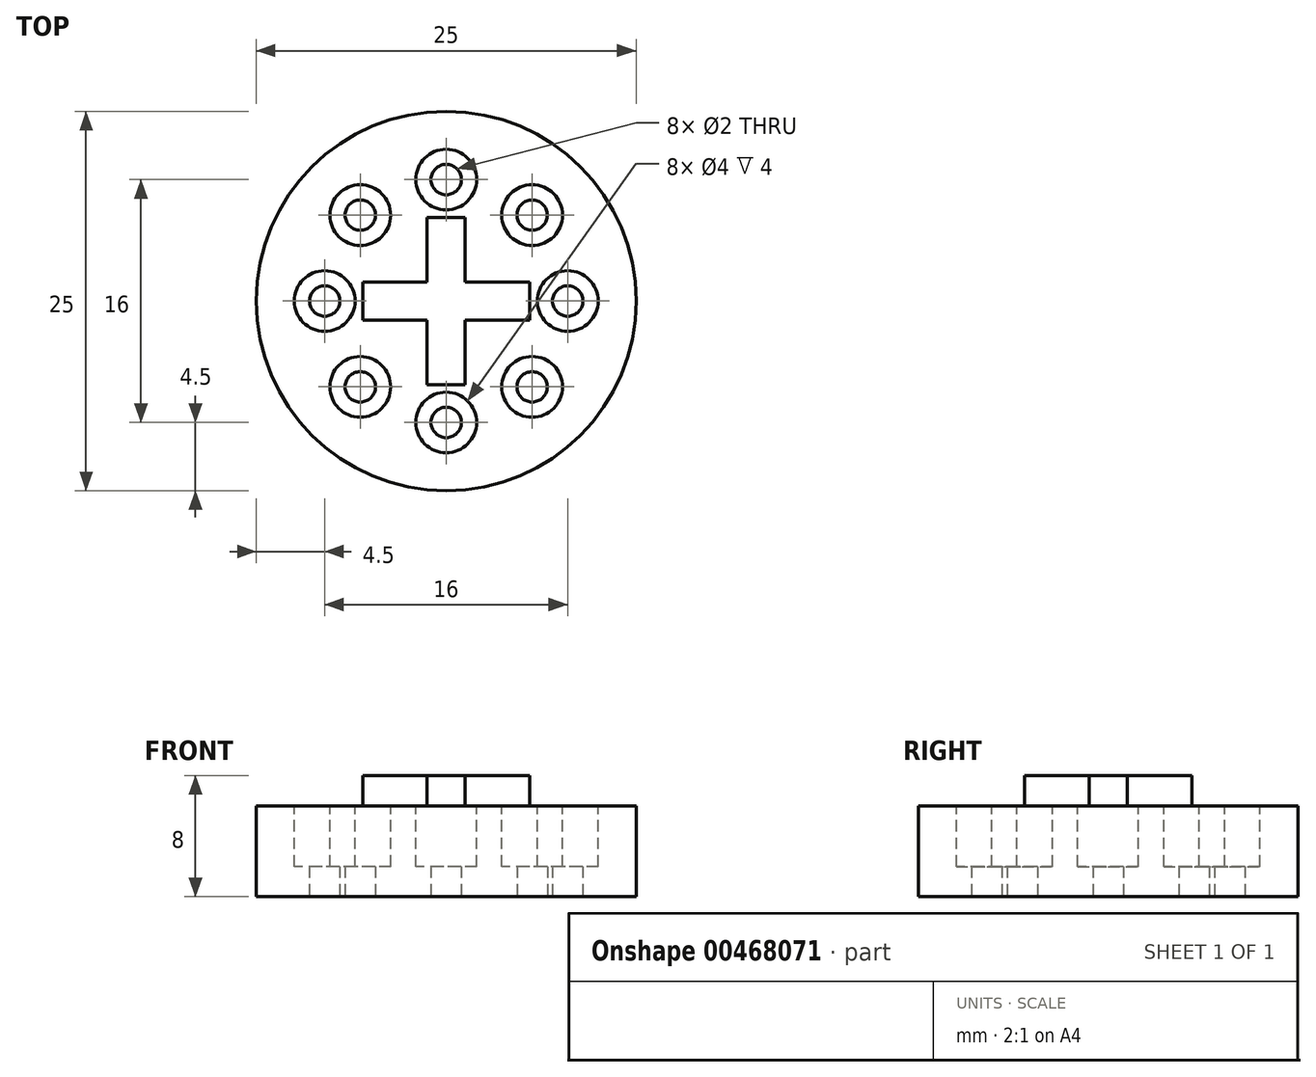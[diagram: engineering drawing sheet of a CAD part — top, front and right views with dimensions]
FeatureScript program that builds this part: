
annotation { "Feature Type Name" : "Feature", "Feature Type Description" : "" }
export const myFeature = defineFeature(function(context is Context, id is Id, definition is map)
    precondition{}
    {
        {
            var Q0;
            Q0=qCreatedBy(makeId("Top.planeOp"),FACE);
            var sketch = newSketch(context, id + "F0", { "sketchPlane" : qUnion([Q0])});
            skCircle(sketch, "E0", {"center": v(0, 0) * mm, "radius": 12.5 * mm});
            skSolve(sketch);
        }
        {
            var Q0;
            Q0 = qSketchRegion(id + "F0", true);
            extrude(context, id + "F1", {"entities" : qUnion([Q0]), "endBound" : BoundingType.SYMMETRIC, "depth" : 6 * mm});
        }
        {
            var Q0;
            Q0=qCreatedBy(makeId("Top.planeOp"),FACE);
            var sketch = newSketch(context, id + "F2", { "sketchPlane" : qUnion([Q0])});
            skCircle(sketch, "E1", {"center": v(0, 0) * mm, "radius": 12.5 * mm});
            skCircle(sketch, "E2", {"center": v(-8, 0) * mm, "radius": 1 * mm});
            skCircle(sketch, "E3.1.0", {"center": v(-5.66, -5.66) * mm, "radius": 1 * mm});
            skCircle(sketch, "E3.2.0", {"center": v(0, -8) * mm, "radius": 1 * mm});
            skCircle(sketch, "E3.3.0", {"center": v(5.66, -5.66) * mm, "radius": 1 * mm});
            skCircle(sketch, "E3.4.0", {"center": v(8, 0) * mm, "radius": 1 * mm});
            skCircle(sketch, "E3.5.0", {"center": v(5.66, 5.66) * mm, "radius": 1 * mm});
            skCircle(sketch, "E3.6.0", {"center": v(0, 8) * mm, "radius": 1 * mm});
            skCircle(sketch, "E3.7.0", {"center": v(-5.66, 5.66) * mm, "radius": 1 * mm});
            skSolve(sketch);
        }
        {
            var Q0;
            Q0=makeQuery(id+"F2.imprint","IMPRINT",FACE,{"disambiguationData":[TD([[makeQuery(id+"F2.imprint","IMPRINT",EDGE,{"derivedFrom":sQuery(id+"F2.wireOp",EDGE,"E3.2.0")}),1.0]])]});
            var Q1;
            Q1=makeQuery(id+"F2.imprint","IMPRINT",FACE,{"disambiguationData":[TD([[makeQuery(id+"F2.imprint","IMPRINT",EDGE,{"derivedFrom":sQuery(id+"F2.wireOp",EDGE,"E3.1.0")}),1.0]])]});
            var Q2;
            Q2=makeQuery(id+"F2.imprint","IMPRINT",FACE,{"disambiguationData":[TD([[makeQuery(id+"F2.imprint","IMPRINT",EDGE,{"derivedFrom":sQuery(id+"F2.wireOp",EDGE,"E2")}),1.0]])]});
            var Q3;
            Q3=makeQuery(id+"F2.imprint","IMPRINT",FACE,{"disambiguationData":[TD([[makeQuery(id+"F2.imprint","IMPRINT",EDGE,{"derivedFrom":sQuery(id+"F2.wireOp",EDGE,"E3.7.0")}),1.0]])]});
            var Q4;
            Q4=makeQuery(id+"F2.imprint","IMPRINT",FACE,{"disambiguationData":[TD([[makeQuery(id+"F2.imprint","IMPRINT",EDGE,{"derivedFrom":sQuery(id+"F2.wireOp",EDGE,"E3.6.0")}),1.0]])]});
            var Q5;
            Q5=makeQuery(id+"F2.imprint","IMPRINT",FACE,{"disambiguationData":[TD([[makeQuery(id+"F2.imprint","IMPRINT",EDGE,{"derivedFrom":sQuery(id+"F2.wireOp",EDGE,"E3.5.0")}),1.0]])]});
            var Q6;
            Q6=makeQuery(id+"F2.imprint","IMPRINT",FACE,{"disambiguationData":[TD([[makeQuery(id+"F2.imprint","IMPRINT",EDGE,{"derivedFrom":sQuery(id+"F2.wireOp",EDGE,"E3.4.0")}),1.0]])]});
            var Q7;
            Q7=makeQuery(id+"F2.imprint","IMPRINT",FACE,{"disambiguationData":[TD([[makeQuery(id+"F2.imprint","IMPRINT",EDGE,{"derivedFrom":sQuery(id+"F2.wireOp",EDGE,"E3.3.0")}),1.0]])]});
            var Q8;
            Q8=sQuery(id+"F2.wireOp",EDGE,"E3.7.0");
            var Q9;
            Q9=sQuery(id+"F2.wireOp",EDGE,"E2");
            var Q10;
            Q10=sQuery(id+"F2.wireOp",EDGE,"E3.6.0");
            var Q11;
            Q11=sQuery(id+"F2.wireOp",EDGE,"E3.5.0");
            var Q12;
            Q12=sQuery(id+"F2.wireOp",EDGE,"E3.4.0");
            var Q13;
            Q13=sQuery(id+"F2.wireOp",EDGE,"E3.2.0");
            var Q14;
            Q14=sQuery(id+"F2.wireOp",EDGE,"E3.3.0");
            var Q15;
            Q15=sQuery(id+"F2.wireOp",EDGE,"E3.1.0");
            extrude(context, id + "F3", {"entities" : qUnion([Q0, Q1, Q2, Q3, Q4, Q5, Q6, Q7]), "operationType" : NewBodyOperationType.REMOVE, "surfaceEntities" : qUnion([Q8, Q9, Q10, Q11, Q12, Q13, Q14, Q15]), "endBound" : BoundingType.SYMMETRIC, "depth" : 25 * mm});
        }
        {
            var Q0;
            Q0=makeQuery(id+"F1.opExtrude","CAP_FACE",FACE,{"disambiguationData":[OSD([sQuery(id+"F0.wireOp",EDGE,"E0")])],"isStart":false});
            var sketch = newSketch(context, id + "F4", { "sketchPlane" : qUnion([Q0])});
            skCircle(sketch, "E4", {"center": v(-5.66, 5.66) * mm, "radius": 2 * mm});
            skCircle(sketch, "E5.1.0", {"center": v(-8, 0) * mm, "radius": 2 * mm});
            skCircle(sketch, "E5.2.0", {"center": v(-5.66, -5.66) * mm, "radius": 2 * mm});
            skCircle(sketch, "E5.3.0", {"center": v(0, -8) * mm, "radius": 2 * mm});
            skCircle(sketch, "E5.4.0", {"center": v(5.66, -5.66) * mm, "radius": 2 * mm});
            skCircle(sketch, "E5.5.0", {"center": v(8, 0) * mm, "radius": 2 * mm});
            skCircle(sketch, "E5.6.0", {"center": v(5.66, 5.66) * mm, "radius": 2 * mm});
            skCircle(sketch, "E5.7.0", {"center": v(0, 8) * mm, "radius": 2 * mm});
            skPoint(sketch, "E5.center", {"position": v(0, 0) * mm});
            skSolve(sketch);
        }
        {
            var Q0;
            Q0=makeQuery(id+"F4.imprint","IMPRINT",FACE,{"disambiguationData":[TD([[makeQuery(id+"F4.imprint","IMPRINT",EDGE,{"derivedFrom":sQuery(id+"F4.wireOp",EDGE,"E4")}),1.0]])]});
            var Q1;
            Q1=makeQuery(id+"F4.imprint","IMPRINT",FACE,{"disambiguationData":[TD([[makeQuery(id+"F4.imprint","IMPRINT",EDGE,{"derivedFrom":sQuery(id+"F4.wireOp",EDGE,"E5.1.0")}),1.0]])]});
            var Q2;
            Q2=makeQuery(id+"F4.imprint","IMPRINT",FACE,{"disambiguationData":[TD([[makeQuery(id+"F4.imprint","IMPRINT",EDGE,{"derivedFrom":sQuery(id+"F4.wireOp",EDGE,"E5.7.0")}),1.0]])]});
            var Q3;
            Q3=makeQuery(id+"F4.imprint","IMPRINT",FACE,{"disambiguationData":[TD([[makeQuery(id+"F4.imprint","IMPRINT",EDGE,{"derivedFrom":sQuery(id+"F4.wireOp",EDGE,"E5.5.0")}),1.0]])]});
            var Q4;
            Q4=makeQuery(id+"F4.imprint","IMPRINT",FACE,{"disambiguationData":[TD([[makeQuery(id+"F4.imprint","IMPRINT",EDGE,{"derivedFrom":sQuery(id+"F4.wireOp",EDGE,"E5.6.0")}),1.0]])]});
            var Q5;
            Q5=makeQuery(id+"F4.imprint","IMPRINT",FACE,{"disambiguationData":[TD([[makeQuery(id+"F4.imprint","IMPRINT",EDGE,{"derivedFrom":sQuery(id+"F4.wireOp",EDGE,"E5.4.0")}),1.0]])]});
            var Q6;
            Q6=makeQuery(id+"F4.imprint","IMPRINT",FACE,{"disambiguationData":[TD([[makeQuery(id+"F4.imprint","IMPRINT",EDGE,{"derivedFrom":sQuery(id+"F4.wireOp",EDGE,"E5.3.0")}),1.0]])]});
            var Q7;
            Q7=makeQuery(id+"F4.imprint","IMPRINT",FACE,{"disambiguationData":[TD([[makeQuery(id+"F4.imprint","IMPRINT",EDGE,{"derivedFrom":sQuery(id+"F4.wireOp",EDGE,"E5.2.0")}),1.0]])]});
            extrude(context, id + "F5", {"entities" : qUnion([Q0, Q1, Q2, Q3, Q4, Q5, Q6, Q7]), "operationType" : NewBodyOperationType.REMOVE, "oppositeDirection" : true, "depth" : 4 * mm});
        }
        {
            var Q0;
            Q0=makeQuery(id+"F1.opExtrude","CAP_FACE",FACE,{"disambiguationData":[OSD([sQuery(id+"F0.wireOp",EDGE,"E0")])],"isStart":false});
            var sketch = newSketch(context, id + "F6", { "sketchPlane" : qUnion([Q0])});
            skLineSegment(sketch, "E6.bottom", {"start": v(-1.25, 5.5) * mm, "end": v(1.25, 5.5) * mm});
            skLineSegment(sketch, "E6.top", {"start": v(-1.25, -5.5) * mm, "end": v(1.25, -5.5) * mm});
            skLineSegment(sketch, "E6.left", {"start": v(-1.25, 5.5) * mm, "end": v(-1.25, -5.5) * mm});
            skLineSegment(sketch, "E6.right", {"start": v(1.25, 5.5) * mm, "end": v(1.25, -5.5) * mm});
            skLineSegment(sketch, "E7.bottom", {"start": v(-5.5, 1.25) * mm, "end": v(5.5, 1.25) * mm});
            skLineSegment(sketch, "E7.top", {"start": v(-5.5, -1.25) * mm, "end": v(5.5, -1.25) * mm});
            skLineSegment(sketch, "E7.left", {"start": v(-5.5, 1.25) * mm, "end": v(-5.5, -1.25) * mm});
            skLineSegment(sketch, "E7.right", {"start": v(5.5, 1.25) * mm, "end": v(5.5, -1.25) * mm});
            skLineSegment(sketch, "E8", {"start": v(-1.25, 5.5) * mm, "end": v(1.25, -5.5) * mm});
            skLineSegment(sketch, "E9", {"start": v(-5.5, -1.25) * mm, "end": v(5.5, 1.25) * mm});
            skSolve(sketch);
        }
        {
            var Q0;
            Q0 = qSketchRegion(id + "F6", true);
            extrude(context, id + "F7", {"entities" : qUnion([Q0]), "operationType" : NewBodyOperationType.ADD, "depth" : 2 * mm});
        }
    });
